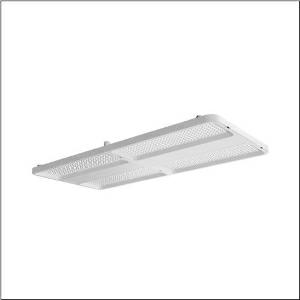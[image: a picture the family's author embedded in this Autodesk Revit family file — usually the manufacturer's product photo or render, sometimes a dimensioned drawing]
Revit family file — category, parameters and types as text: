
# Revit family: highbay_11_maxi_51hn11db4hda
name_source: partatom
category: Lighting Fixtures
units: mm (PartAtom-declared; Revit-internal decimal feet)

## family parameters
Cut with Voids When Loaded = No
Host = Face
Light Source = No
Part Type = Normal
Room Calculation Point = No
Round Connector Dimension = Use Diameter
Shared = No

## types (1)
- --- (1 x LED, 2990 lm, 15.1 W, 4000K)
    Apparent Load = 15 VA
    CIE Flux Codes = 85 97 100 100 100
    Color Rendering = 80
    Color Temperature = 4000K
    Default Elevation = 1800 mm
    Description = high bay luminaire Highbay 11 maxi; direct symmetric narrow distribution, light control with lens of PMMA; UGR ≤ 19 (X = 4H | Y = 8H | S = 0.25H | reflection values 70/50/20); luminous flux: 20.000lm; light colour: 840, colour temperature: 4000K, MacAdam ≤ 2 SDCM (initial), colour rendering: CRI > 80; luminous efficacy: 210,7lm/W; rated service life: 100.000h (L95) at AT= 25°C; control: DALI 2; luminaire connection: terminal, 5-pole, max. 2.5mm² (cable entry for one cable, Ø 8.5..16mm); mains connection: 230..240V, AC/DC 0/50..60Hz; connected load: 94,9W; protection rating (complete): IP66; insulation class (complete): insulation class I (protective earthing); protection symbol: D; impact resistance: IK08; certification: CE, ENEC, VDE, UKCA; luminaire for central battery installations according to EN 60598-2-22, internal wiring halogen-free; luminaire Suitable for use in the food industry according to the specifications of IFS-Food, HACCP and/or BRC; LABS conformity tested according to VDMA 24364:2018-05; housing frame of high-performance plastic PA6, matt traffic white (RAL 9016); cover of PMMA; dimension (LxWxH): 946 x 442 x 72mm; permissible operating ambient temperature: -40..+65°C (reducing of maximum allowable ambient temperature of 5°C with ceiling mounting); packaging unit: 1 piece; (delivery without accessories; please order mounting accessories separately)
    Height = 72 mm  [stored 0.23622 ft]
    Lamp = 1 x LED
    Lamp Light Flux = 2990 lm
    Lamp Power = 15.1 W
    Lamp count = 1
    Length = 946 mm
    Luminous efficacy = 198 lm/W
    Manufacturer = Siteco
    ModVariant = No
    Model = 51HN11DB4HDA
    Mounting Place = Ceiling
    Mounting Type = Pendant
    Number of Poles = 1
    OnlyDefault = Yes
    Power Factor = 1
    Product Name = Highbay 11 maxi
    Product group = high bay luminaire
    ProductGroupID = 902
    Protection Class = Protection class I
    Protection Degree = IP 66
    RLX_Detail_Level = 1
    RLX_Emergency_Light_Flux = 0 lm
    RLX_Emergency_Type = 0
    RLX_Emergency_Type_DB = No
    RlxData = <blob elided: 127385 chars, md5=a88ab7e2>
    Socket = socket
    Standby Power = 0 W
    System Light Flux = 2990 lm
    System Power = 15 W
    Type Comments = : DC mode (central or group accumulator) initial emergency light level
    Type Image = l_1363244.jpg
    URL = http://relux.com
    VarID = @adj_022147
    Voltage = 0 V
    Weight = 0.00 kg
    Width = 442 mm

note: [stored X ft] marks values corroborated as IEEE doubles in the binary element streams (Revit-internal decimal feet)

## geometry (parser evidence)
native form markers: Blend x4, Sweep x11
no freeform markers — native parametric forms only
